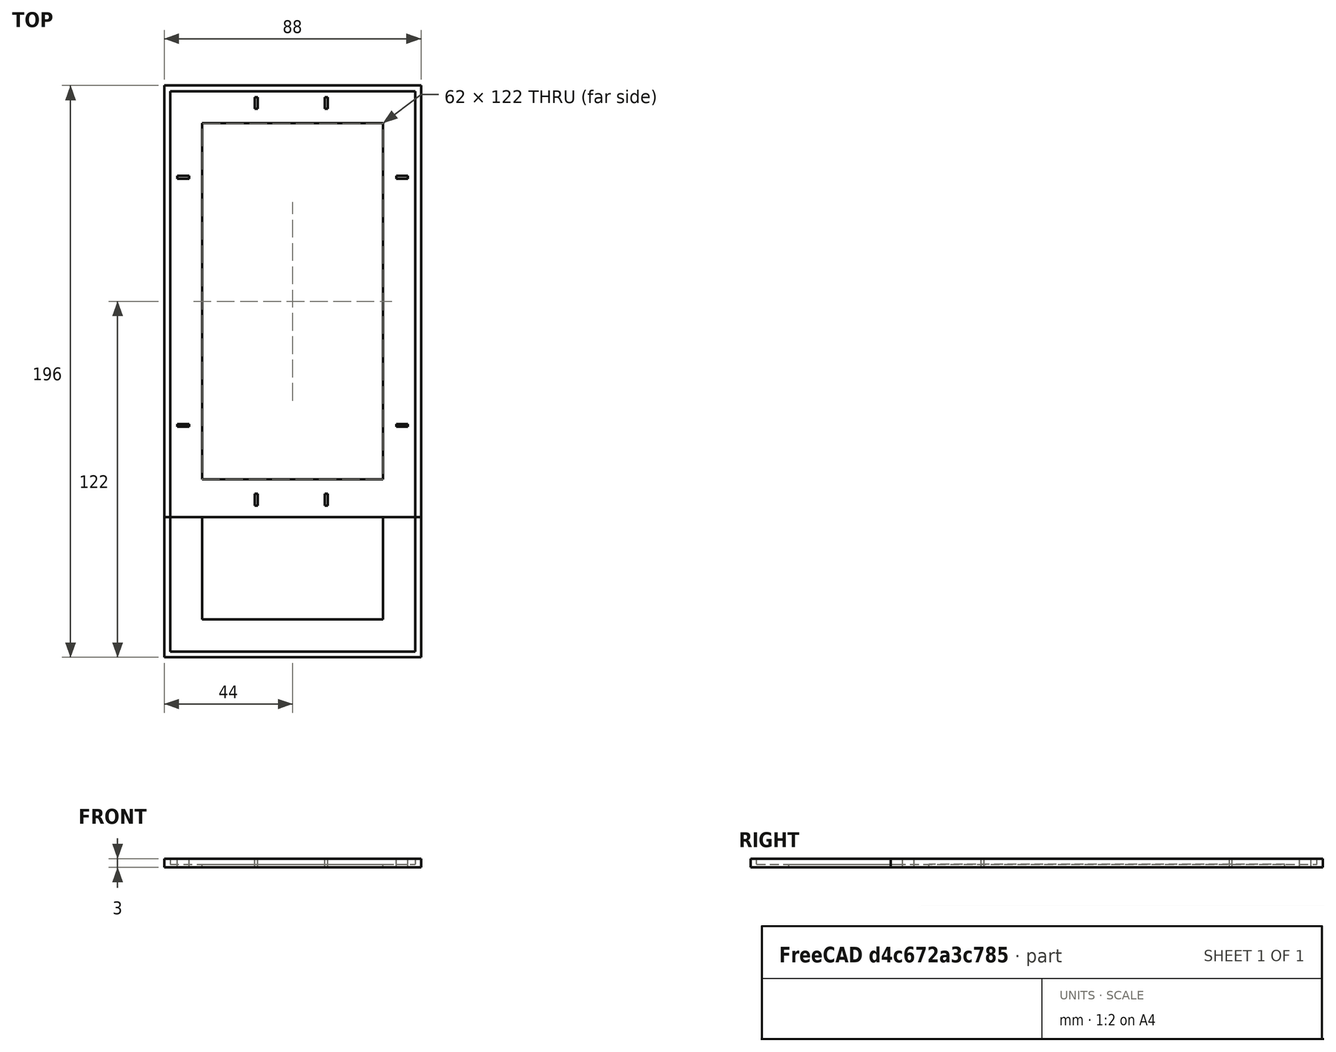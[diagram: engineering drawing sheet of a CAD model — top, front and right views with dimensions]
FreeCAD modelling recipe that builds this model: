
FCSTD DOCUMENT  (FreeCAD 0.16R)
Label: sonoff-T1-US-aufputz-und-Steckdose_v2.4_Adapter
License: All rights reserved
LicenseURL: http://en.wikipedia.org/wiki/All_rights_reserved
objects: Part::Box×14, Part::Cut×5
note: 19 computed .brp shape members not serialized (recipe doc carries the construction recipe); baked Part::Feature solids carry a one-line shape summary decoded from their .brp

FEATURE [Part::Box] Box  label="Cube"
  Height = 3
  Length = 88
  Width = 148
FEATURE [Part::Box] Box001  label="Cube001"
  Height = 3
  Length = 62
  Placement = pos=(13,13,0) rot=(0,0,1;0rad)
  Width = 122
FEATURE [Part::Cut] Cut
  Base = -> Box
  Tool = -> Box001
FEATURE [Part::Box] Box002  label="Cube002"
  Height = 2
  Length = 84
  Placement = pos=(2,2,1) rot=(0,0,1;0rad)
  Width = 144
FEATURE [Part::Cut] Cut001
  Base = -> Cut
  Tool = -> Box002
FEATURE [Part::Box] Box003  label="Cube003"
  Height = 3
  Length = 4
  Placement = pos=(4.5,31,0) rot=(0,0,1;0rad)
  Width = 1
FEATURE [Part::Box] Box004  label="Cube004"
  Height = 3
  Length = 4
  Placement = pos=(79.5,31,0) rot=(0,0,1;0rad)
  Width = 1
FEATURE [Part::Box] Box005  label="Cube005"
  Height = 3
  Length = 4
  Placement = pos=(4.5,116,0) rot=(0,0,1;0rad)
  Width = 1
FEATURE [Part::Box] Box006  label="Cube006"
  Height = 3
  Length = 4
  Placement = pos=(79.5,116,0) rot=(0,0,1;0rad)
  Width = 1
FEATURE [Part::Box] Box007  label="Cube007"
  Height = 3
  Length = 1
  Placement = pos=(31,4,0) rot=(0,0,1;0rad)
  Width = 4
FEATURE [Part::Box] Box008  label="Cube008"
  Height = 3
  Length = 1
  Placement = pos=(55,4,0) rot=(0,0,1;0rad)
  Width = 4
FEATURE [Part::Box] Box009  label="Cube009"
  Height = 3
  Length = 1
  Placement = pos=(31,140,0) rot=(0,0,1;0rad)
  Width = 4
FEATURE [Part::Box] Box010  label="Cube010"
  Height = 3
  Length = 1
  Placement = pos=(55,140,0) rot=(0,0,1;0rad)
  Width = 4
FEATURE [Part::Box] Box011  label="Cube011"
  Height = 3
  Length = 88
  Placement = pos=(0,-48,0) rot=(0,0,1;0rad)
  Width = 48
FEATURE [Part::Box] Box012  label="Cube012"
  Height = 2
  Length = 84
  Placement = pos=(2,-46,1) rot=(0,0,1;0rad)
  Width = 48
FEATURE [Part::Cut] Cut002
  Base = -> Box011
  Tool = -> Box012
FEATURE [Part::Cut] Cut003
  Base = -> Cut001
  Tool = -> Box012
FEATURE [Part::Box] Box013  label="Cube013"
  Height = 3
  Length = 62
  Placement = pos=(13,-35,0) rot=(0,0,1;0rad)
  Width = 35
FEATURE [Part::Cut] Cut004
  Base = -> Cut002
  Tool = -> Box013
